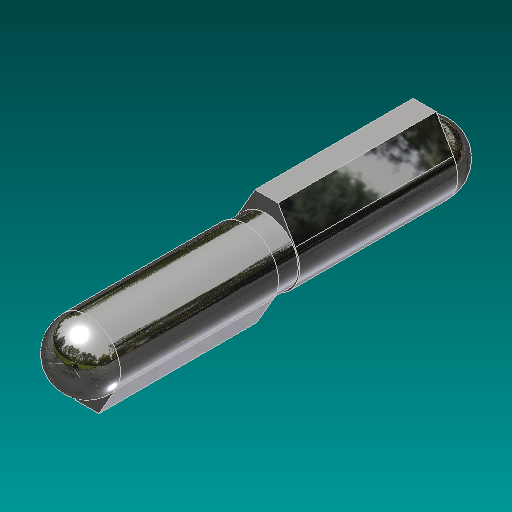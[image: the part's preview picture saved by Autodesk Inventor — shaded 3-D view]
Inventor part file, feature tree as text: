
AUTODESK INVENTOR PART (.ipt)
format: ipt  version: 2017 (Build 210142000, 142)  size: 200,704 bytes
history: native  units: in
note: dims shown in document units (in); Inventor stores cm internally (conversion verified against a paired STEP export)
features: sketch x4, extrude x3, revolve x1
ambient origin geometry x8: Origin, YZ Plane, XZ Plane, XY Plane, X Axis, Y Axis, Z Axis, Center Point
bodies: Solid1 (feature_tree)
feature tree (8):
  extrude  "Extrusion1"  Depth=0.125in TaperAngle=0.0deg
  extrude  "Extrusion2"  Depth=0.9375in TaperAngle=0.0deg
  extrude  "Extrusion3"  TaperAngle=90.0deg  [1 undecoded]
  revolve  "Revolution1"  [1 undecoded]
  sketch  "Sketch1"  dims[d0=0.375in d1=0.125in d2=0.0in]
  sketch  "Sketch2"  dims[d4=60.0deg d5=0.9375in d6=0.0in]
  sketch  "Sketch3"  dims[d7=0.9375in d8=0.0in d9=90.0deg]
  sketch  "Sketch4"  dims[d10=0.4724in d12=0.3937in d13=0.3937in]
note: 2 required parameter values undecoded (feature->parameter linkage not recoverable at this tier; creation-order binding heuristic only, values carry confidence <= 0.55)